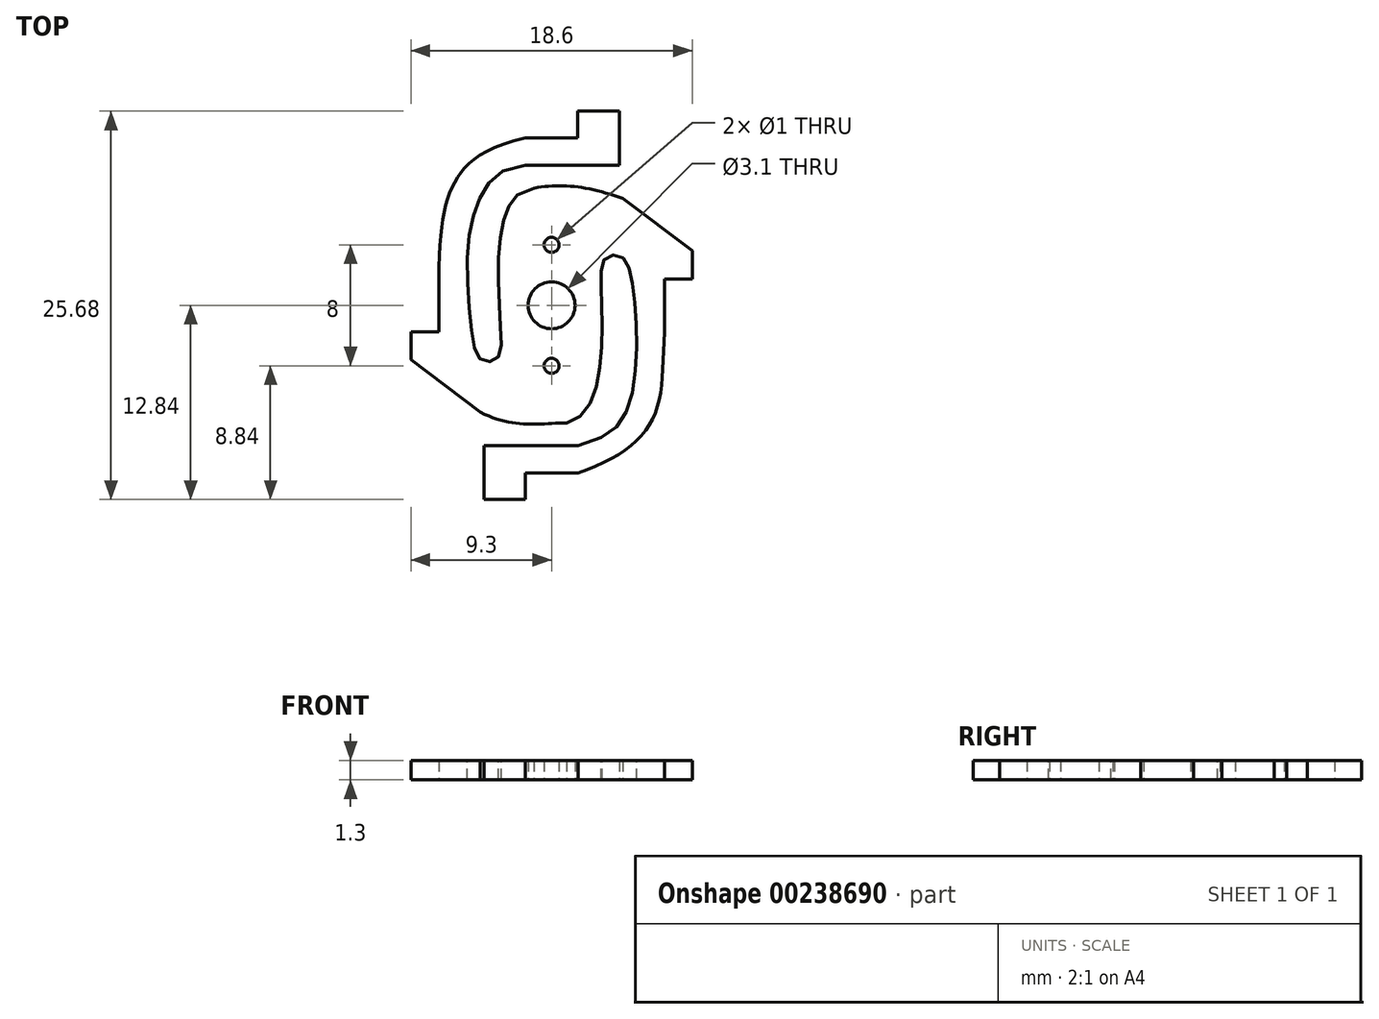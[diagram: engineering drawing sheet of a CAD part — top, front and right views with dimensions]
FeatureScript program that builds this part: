
annotation { "Feature Type Name" : "Feature", "Feature Type Description" : "" }
export const myFeature = defineFeature(function(context is Context, id is Id, definition is map)
    precondition{}
    {
        {
            var Q0;
            Q0=qCreatedBy(makeId("Top.planeOp"),FACE);
            var sketch = newSketch(context, id + "F0", { "sketchPlane" : qUnion([Q0])});
            skPoint(sketch, "E0", {"position": v(-3.7, 0) * mm});
            skPoint(sketch, "E1", {"position": v(3.7, 0) * mm});
            skCircle(sketch, "E2", {"center": v(0, 0) * mm, "radius": 1.55 * mm});
            skCircle(sketch, "E3", {"center": v(0, 0) * mm, "radius": 11.07 * mm, "construction": true});
            skCircle(sketch, "E4", {"center": v(0, 0) * mm, "radius": 7.46 * mm, "construction": true});
            skLineSegment(sketch, "E5", {"start": v(1.74, 11.07) * mm, "end": v(-1.74, 11.07) * mm});
            skLineSegment(sketch, "E6", {"start": v(1.74, 11.07) * mm, "end": v(1.74, 12.84) * mm});
            skLineSegment(sketch, "E7", {"start": v(1.74, 12.84) * mm, "end": v(4.48, 12.84) * mm});
            skLineSegment(sketch, "E8", {"start": v(4.48, 12.84) * mm, "end": v(4.48, 9.27) * mm});
            skLineSegment(sketch, "E9", {"start": v(4.48, 9.27) * mm, "end": v(-1.74, 9.27) * mm});
            skLineSegment(sketch, "E10", {"start": v(-7.45, 1.74) * mm, "end": v(-7.46, -1.74) * mm});
            skLineSegment(sketch, "E11", {"start": v(-7.46, -1.74) * mm, "end": v(-9.3, -1.74) * mm});
            skLineSegment(sketch, "E12", {"start": v(-9.3, -1.74) * mm, "end": v(-9.3, -3.6) * mm});
            skCircle(sketch, "E13", {"center": v(0, 4) * mm, "radius": 0.5 * mm});
            skCircle(sketch, "E14.MirrorC", {"center": v(0, -4) * mm, "radius": 0.5 * mm});
            skFitSpline(sketch, "E15", {"points": [v(-1.74, 11.07) * mm, v(-6.43, 8.1) * mm, v(-7.45, 1.74) * mm], "startDerivative": vector(-18.62, -4.56) * mm, "endDerivative": vector(-0.19, -19.3) * mm});
            skFitSpline(sketch, "E16", {"points": [v(-1.74, 9.27) * mm, v(-4.64, 7.29) * mm, v(-5.55, 3.52) * mm, v(-5.24, -2) * mm, v(-4.63, -3.61) * mm, v(-3.62, -3.53) * mm, v(-3.36, -1.71) * mm, v(-3.5, 3.3) * mm, v(-2.9, 6.38) * mm, v(-1.16, 7.75) * mm], "startDerivative": vector(-41.9, -3.29) * mm, "endDerivative": vector(35.28, 7.09) * mm});
            skLineSegment(sketch, "E17", {"start": v(-9.3, -3.6) * mm, "end": v(-4.71, -7.07) * mm});
            skLineSegment(sketch, "E18.1.1", {"start": v(-1.73, -12.84) * mm, "end": v(-4.48, -12.84) * mm});
            skLineSegment(sketch, "E18.1.2", {"start": v(-4.48, -12.84) * mm, "end": v(-4.48, -9.27) * mm});
            skLineSegment(sketch, "E18.1.3", {"start": v(-4.48, -9.27) * mm, "end": v(1.75, -9.27) * mm});
            skLineSegment(sketch, "E18.1.4", {"start": v(9.3, 3.61) * mm, "end": v(4.72, 7.07) * mm});
            skLineSegment(sketch, "E18.1.5", {"start": v(-1.73, -11.07) * mm, "end": v(1.75, -11.07) * mm});
            skLineSegment(sketch, "E18.1.6", {"start": v(7.46, 1.74) * mm, "end": v(9.3, 1.74) * mm});
            skLineSegment(sketch, "E18.1.8", {"start": v(-1.73, -11.07) * mm, "end": v(-1.73, -12.84) * mm});
            skLineSegment(sketch, "E18.1.9", {"start": v(9.3, 1.74) * mm, "end": v(9.3, 3.61) * mm});
            skLineSegment(sketch, "E18.1.11", {"start": v(7.46, -1.74) * mm, "end": v(7.46, 1.74) * mm});
            skFitSpline(sketch, "E19", {"points": [v(1.75, -11.07) * mm, v(6.55, -7.76) * mm, v(7.46, -1.74) * mm], "startDerivative": vector(14.06, 4.68) * mm, "endDerivative": vector(0.68, 15.7) * mm});
            skFitSpline(sketch, "E20", {"points": [v(1.75, -9.27) * mm, v(4.93, -7.08) * mm, v(5.62, -2.3) * mm, v(5.26, 1.9) * mm, v(4.58, 3.23) * mm, v(3.56, 3.12) * mm, v(3.28, 1.5) * mm, v(3.31, -2.33) * mm, v(2.69, -6.16) * mm, v(1, -7.77) * mm], "startDerivative": vector(42.55, 10.16) * mm, "endDerivative": vector(-23.47, -3.48) * mm});
            skFitSpline(sketch, "E21", {"points": [v(1, -7.77) * mm, v(-4.71, -7.07) * mm], "startDerivative": vector(-5.76, -0.12) * mm, "endDerivative": vector(-6.58, 3.3) * mm});
            skFitSpline(sketch, "E22", {"points": [v(-1.16, 7.75) * mm, v(4.72, 7.07) * mm], "startDerivative": vector(5.61, 1.06) * mm, "endDerivative": vector(6.9, -2.41) * mm});
            skSolve(sketch);
        }
        {
            var Q0;
            Q0=makeQuery(id+"F0.imprint","IMPRINT",FACE,{"disambiguationData":[TD([[makeQuery(id+"F0.imprint","IMPRINT",EDGE,{"derivedFrom":sQuery(id+"F0.wireOp",EDGE,"E2")}),-1.0]])]});
            extrude(context, id + "F1", {"entities" : qUnion([Q0]), "depth" : 1.3 * mm});
        }
    });
